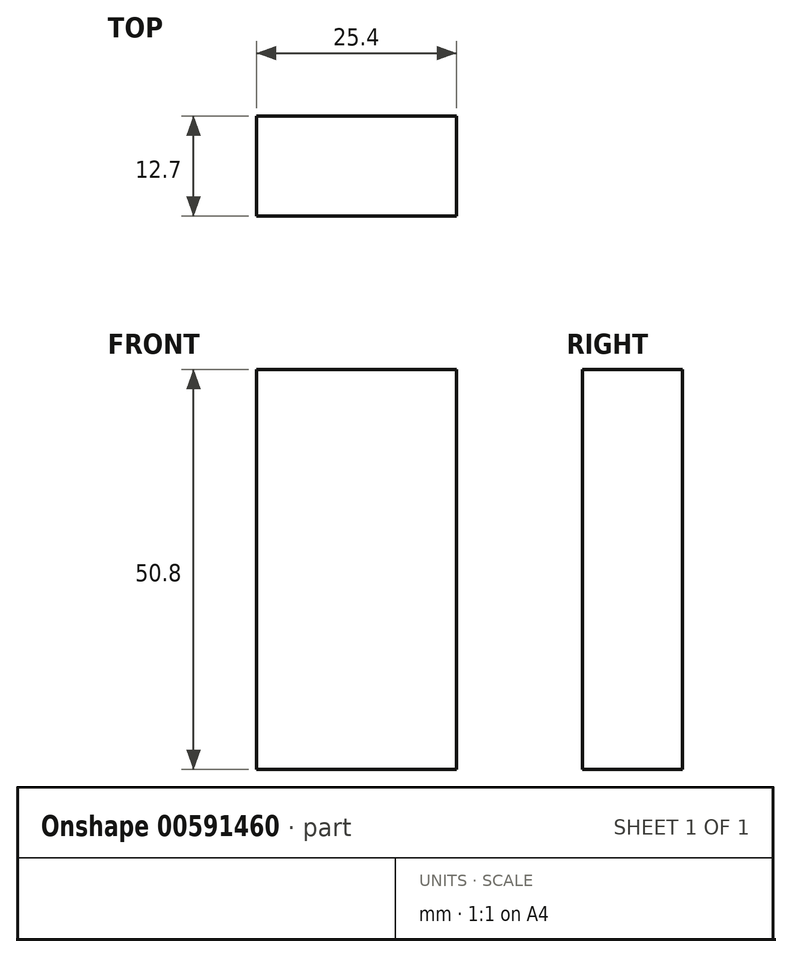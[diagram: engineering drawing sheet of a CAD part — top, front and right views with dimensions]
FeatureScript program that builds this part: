
annotation { "Feature Type Name" : "Feature", "Feature Type Description" : "" }
export const myFeature = defineFeature(function(context is Context, id is Id, definition is map)
    precondition{}
    {
        {
            var Q0;
            Q0=qCreatedBy(makeId("Front.planeOp"),FACE);
            var sketch = newSketch(context, id + "F0", { "sketchPlane" : qUnion([Q0])});
            skLineSegment(sketch, "E0.bottom", {"start": v(0, 0) * mm, "end": v(25.4, 0) * mm});
            skLineSegment(sketch, "E0.top", {"start": v(0, 50.8) * mm, "end": v(25.4, 50.8) * mm});
            skLineSegment(sketch, "E0.left", {"start": v(0, 0) * mm, "end": v(0, 50.8) * mm});
            skLineSegment(sketch, "E0.right", {"start": v(25.4, 0) * mm, "end": v(25.4, 50.8) * mm});
            skSolve(sketch);
        }
        {
            var Q0;
            Q0=makeQuery(id+"F0.imprint","IMPRINT",FACE,{"disambiguationData":[TD([[makeQuery(id+"F0.imprint","IMPRINT",EDGE,{"derivedFrom":sQuery(id+"F0.wireOp",EDGE,"E0.bottom")}),1.0]])]});
            extrude(context, id + "F1", {"entities" : qUnion([Q0]), "depth" : 12.7 * mm, "offsetDistance" : 25.4 * mm});
        }
    });
